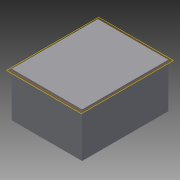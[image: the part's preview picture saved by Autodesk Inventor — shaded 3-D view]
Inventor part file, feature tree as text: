
AUTODESK INVENTOR PART (.ipt)
format: ipt  version: 2014 (Build 180170000, 170)  size: 99,328 bytes
history: native  units: mm
features: plane x3, extrude x3, sketch x3, reference x1
ambient origin geometry x8: Origin, YZ Plane, XZ Plane, XY Plane, X Axis, Y Axis, Z Axis, Center Point
bodies: Volumenkörper1 (feature_tree)
feature tree (10):
  plane  "Arbeitsebene1"
  extrude  "Extrusion1"  Depth=1.0mm TaperAngle=0.0deg
  sketch  "Skizze2"  dims[d3=1.0mm d4=1.0mm d5=0.0mm]
  plane  "Arbeitsebene2"
  plane  "Arbeitsebene3"
  extrude  "Extrusion2"  Depth=1.0mm TaperAngle=0.0deg
  extrude  "Extrusion3"  Depth=1.0mm TaperAngle=0.0deg
  sketch  "Skizze1"  dims[d0=1.1mm d1=1.0mm d2=0.0mm]
  reference  "Referenz1"
  sketch  "Skizze3"  dims[d6=20.0mm d7=1.0mm d8=0.0mm]
